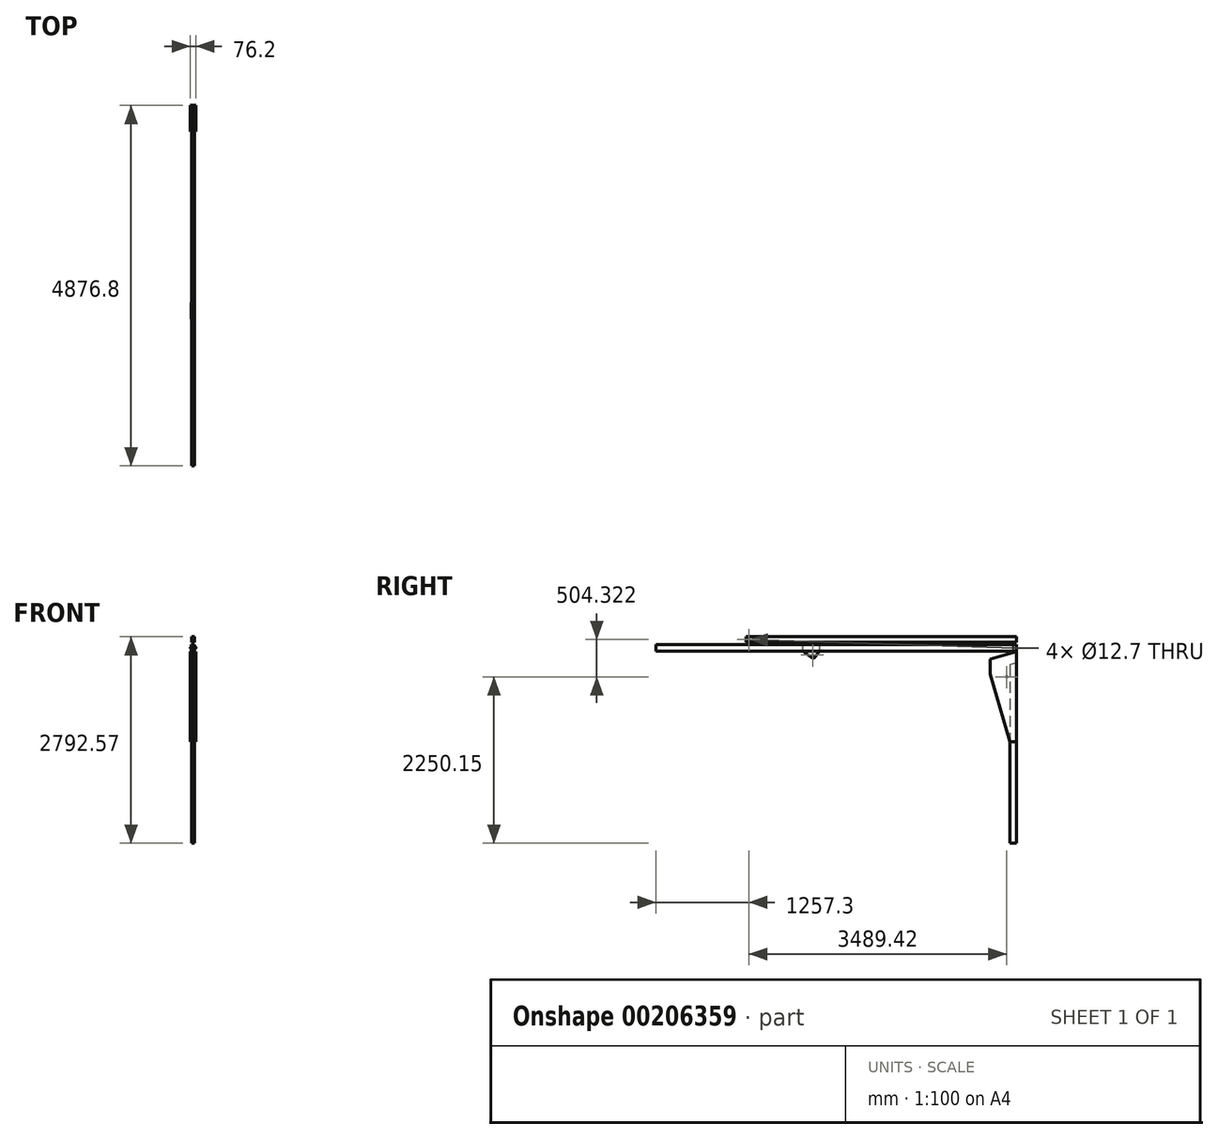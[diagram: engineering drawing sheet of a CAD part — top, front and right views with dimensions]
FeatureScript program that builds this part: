
annotation { "Feature Type Name" : "Feature", "Feature Type Description" : "" }
export const myFeature = defineFeature(function(context is Context, id is Id, definition is map)
    precondition{}
    {
        {
            var Q0;
            Q0=qCreatedBy(makeId("Right.planeOp"),FACE);
            var sketch = newSketch(context, id + "F0", { "sketchPlane" : qUnion([Q0])});
            skLineSegment(sketch, "E0", {"start": v(-355.6, 0) * mm, "end": v(0, 99.35) * mm});
            skLineSegment(sketch, "E1", {"start": v(0, 99.35) * mm, "end": v(0, -1119.85) * mm});
            skLineSegment(sketch, "E2", {"start": v(0, -1119.85) * mm, "end": v(-88.9, -1119.85) * mm});
            skLineSegment(sketch, "E3", {"start": v(-355.6, 0) * mm, "end": v(-355.6, -203.2) * mm});
            skLineSegment(sketch, "E4", {"start": v(-355.6, -203.2) * mm, "end": v(-88.9, -1119.85) * mm});
            skSolve(sketch);
        }
        {
            var Q0;
            Q0 = qSketchRegion(id + "F0", true);
            extrude(context, id + "F1", {"entities" : qUnion([Q0]), "depth" : 76.2 * mm});
        }
        {
            var Q0;
            Q0=makeQuery(id+"F1.opExtrude","SWEPT_FACE",FACE,{"disambiguationData":[OSD([sQuery(id+"F0.wireOp",EDGE,"E1")])]});
            var sketch = newSketch(context, id + "F2", { "sketchPlane" : qUnion([Q0])});
            skLineSegment(sketch, "E5.bottom", {"start": v(-57.15, 99.35) * mm, "end": v(-19.05, 99.35) * mm});
            skLineSegment(sketch, "E5.top", {"start": v(-57.15, -53.05) * mm, "end": v(-19.05, -53.05) * mm});
            skLineSegment(sketch, "E5.left", {"start": v(-57.15, 99.35) * mm, "end": v(-57.15, -53.05) * mm});
            skLineSegment(sketch, "E5.right", {"start": v(-19.05, 99.35) * mm, "end": v(-19.05, -53.05) * mm});
            skLineSegment(sketch, "E6", {"start": v(-57.15, -53.05) * mm, "end": v(-76.2, -53.05) * mm, "construction": true});
            skLineSegment(sketch, "E7", {"start": v(-19.05, -53.05) * mm, "end": v(0, -53.05) * mm, "construction": true});
            skSolve(sketch);
        }
        {
            var Q0;
            Q0 = qSketchRegion(id + "F2", true);
            var Q1;
            Q1=makeQuery(id+"F1.opExtrude","CAP_EDGE",EDGE,{"disambiguationData":[OSD([sQuery(id+"F0.wireOp",EDGE,"E0")])],"isStart":false});
            sweep(context, id + "F3", {"operationType" : NewBodyOperationType.REMOVE, "profiles" : qUnion([Q0]), "path" : qUnion([Q1])});
        }
        {
            var Q0;
            Q0=makeQuery(id+"F1.opExtrude","SWEPT_FACE",FACE,{"disambiguationData":[OSD([sQuery(id+"F0.wireOp",EDGE,"E2")])]});
            var sketch = newSketch(context, id + "F4", { "sketchPlane" : qUnion([Q0])});
            skLineSegment(sketch, "E8.bottom", {"start": v(19.05, 88.9) * mm, "end": v(57.15, 88.9) * mm});
            skLineSegment(sketch, "E8.top", {"start": v(19.05, 355.6) * mm, "end": v(57.15, 355.6) * mm});
            skLineSegment(sketch, "E8.left", {"start": v(19.05, 88.9) * mm, "end": v(19.05, 355.6) * mm});
            skLineSegment(sketch, "E8.right", {"start": v(57.15, 88.9) * mm, "end": v(57.15, 355.6) * mm});
            skLineSegment(sketch, "E9", {"start": v(0, 88.9) * mm, "end": v(19.05, 88.9) * mm, "construction": true});
            skLineSegment(sketch, "E10", {"start": v(57.15, 88.9) * mm, "end": v(76.2, 88.9) * mm, "construction": true});
            skSolve(sketch);
        }
        {
            var Q0;
            Q0 = qSketchRegion(id + "F4", true);
            extrude(context, id + "F5", {"entities" : qUnion([Q0]), "operationType" : NewBodyOperationType.REMOVE, "endBound" : BoundingType.THROUGH_ALL, "oppositeDirection" : true, "depth" : 30.48 * mm});
        }
        {
            var Q0;
            Q0=makeQuery(id+"F1.opExtrude","SWEPT_FACE",FACE,{"disambiguationData":[OSD([sQuery(id+"F0.wireOp",EDGE,"E2")])]});
            var sketch = newSketch(context, id + "F6", { "sketchPlane" : qUnion([Q0])});
            skLineSegment(sketch, "E11.bottom", {"start": v(19.05, 88.9) * mm, "end": v(57.15, 88.9) * mm});
            skLineSegment(sketch, "E11.top", {"start": v(19.05, 0) * mm, "end": v(57.15, 0) * mm});
            skLineSegment(sketch, "E11.left", {"start": v(19.05, 88.9) * mm, "end": v(19.05, 0) * mm});
            skLineSegment(sketch, "E11.right", {"start": v(57.15, 88.9) * mm, "end": v(57.15, 0) * mm});
            skSolve(sketch);
        }
        {
            var Q0;
            Q0 = qSketchRegion(id + "F6", true);
            extrude(context, id + "F7", {"entities" : qUnion([Q0]), "operationType" : NewBodyOperationType.ADD, "depth" : 1371.6 * mm});
        }
        {
            var Q0;
            Q0=makeQuery(id+"F1.opExtrude","CAP_FACE",FACE,{"disambiguationData":[OSD([sQuery(id+"F0.wireOp",EDGE,"E0"),sQuery(id+"F0.wireOp",EDGE,"E1"),sQuery(id+"F0.wireOp",EDGE,"E2"),sQuery(id+"F0.wireOp",EDGE,"E3"),sQuery(id+"F0.wireOp",EDGE,"E4")])],"isStart":true});
            var sketch = newSketch(context, id + "F8", { "sketchPlane" : qUnion([Q0])});
            skLineSegment(sketch, "E12", {"start": v(355.6, -203.2) * mm, "end": v(76.2, -203.2) * mm, "construction": true});
            skLineSegment(sketch, "E13", {"start": v(76.2, -203.2) * mm, "end": v(76.2, -279.4) * mm, "construction": true});
            skPoint(sketch, "E14.first.point", {"position": v(76.2, -241.3) * mm});
            skCircle(sketch, "E15", {"center": v(130.08, -241.3) * mm, "radius": 6.35 * mm});
            skLineSegment(sketch, "E16", {"start": v(76.2, -241.3) * mm, "end": v(38.1, -241.3) * mm, "construction": true});
            skLineSegment(sketch, "E17", {"start": v(38.1, -241.3) * mm, "end": v(38.1, -203.2) * mm, "construction": true});
            skLineSegment(sketch, "E18", {"start": v(38.1, -203.2) * mm, "end": v(76.2, -241.3) * mm, "construction": true});
            skLineSegment(sketch, "E19", {"start": v(76.2, -241.3) * mm, "end": v(130.08, -241.3) * mm, "construction": true});
            skSolve(sketch);
        }
        {
            var Q0;
            Q0 = qSketchRegion(id + "F8", true);
            extrude(context, id + "F9", {"entities" : qUnion([Q0]), "operationType" : NewBodyOperationType.REMOVE, "endBound" : BoundingType.THROUGH_ALL, "oppositeDirection" : true, "depth" : 30.48 * mm});
        }
        {
            var Q0;
            Q0=qCreatedBy(makeId("Front.planeOp"),FACE);
            var sketch = newSketch(context, id + "F10", { "sketchPlane" : qUnion([Q0])});
            skLineSegment(sketch, "E20.bottom", {"start": v(19.05, 196.76) * mm, "end": v(57.15, 196.76) * mm});
            skLineSegment(sketch, "E20.top", {"start": v(19.05, 107.86) * mm, "end": v(57.15, 107.86) * mm});
            skLineSegment(sketch, "E20.left", {"start": v(19.05, 196.76) * mm, "end": v(19.05, 107.86) * mm});
            skLineSegment(sketch, "E20.right", {"start": v(57.15, 196.76) * mm, "end": v(57.15, 107.86) * mm});
            skSolve(sketch);
        }
        {
            var Q0;
            Q0 = qSketchRegion(id + "F10", true);
            extrude(context, id + "F11", {"entities" : qUnion([Q0]), "depth" : 4876.8 * mm});
        }
        {
            var Q0;
            Q0=makeQuery(id+"F11.opExtrude","SWEPT_FACE",FACE,{"disambiguationData":[OSD([sQuery(id+"F10.wireOp",EDGE,"E20.left")])]});
            var sketch = newSketch(context, id + "F12", { "sketchPlane" : qUnion([Q0])});
            skLineSegment(sketch, "E21", {"start": v(0, 152.31) * mm, "end": v(44.45, 152.31) * mm, "construction": true});
            skLineSegment(sketch, "E22", {"start": v(44.45, 152.31) * mm, "end": v(44.45, 196.76) * mm, "construction": true});
            skCircle(sketch, "E23", {"center": v(44.45, 152.31) * mm, "radius": 6.35 * mm});
            skSolve(sketch);
        }
        {
            var Q0;
            Q0 = qSketchRegion(id + "F12", true);
            extrude(context, id + "F13", {"entities" : qUnion([Q0]), "operationType" : NewBodyOperationType.ADD, "depth" : 19.05 * mm});
        }
        {
            var Q0;
            Q0=makeQuery(id+"F11.opExtrude","SWEPT_FACE",FACE,{"disambiguationData":[OSD([sQuery(id+"F10.wireOp",EDGE,"E20.right")])]});
            var sketch = newSketch(context, id + "F14", { "sketchPlane" : qUnion([Q0])});
            skLineSegment(sketch, "E24", {"start": v(0, 152.31) * mm, "end": v(-44.45, 152.31) * mm, "construction": true});
            skLineSegment(sketch, "E25", {"start": v(-44.45, 152.31) * mm, "end": v(-44.45, 196.76) * mm, "construction": true});
            skCircle(sketch, "E26", {"center": v(-44.45, 152.31) * mm, "radius": 6.35 * mm});
            skSolve(sketch);
        }
        {
            var Q0;
            Q0 = qSketchRegion(id + "F14", true);
            extrude(context, id + "F15", {"entities" : qUnion([Q0]), "operationType" : NewBodyOperationType.ADD, "depth" : 19.05 * mm});
        }
        {
            var Q0;
            Q0=makeQuery(id+"F11.opExtrude","SWEPT_FACE",FACE,{"disambiguationData":[OSD([sQuery(id+"F10.wireOp",EDGE,"E20.left")])]});
            var sketch = newSketch(context, id + "F16", { "sketchPlane" : qUnion([Q0])});
            skLineSegment(sketch, "E27", {"start": v(2664.97, 107.86) * mm, "end": v(2748.51, 0.51) * mm});
            skLineSegment(sketch, "E28", {"start": v(2748.51, 0.51) * mm, "end": v(2886.46, 107.86) * mm});
            skLineSegment(sketch, "E29", {"start": v(2886.46, 107.86) * mm, "end": v(2886.46, 196.76) * mm});
            skLineSegment(sketch, "E30", {"start": v(2886.46, 196.76) * mm, "end": v(2664.97, 196.76) * mm});
            skLineSegment(sketch, "E31", {"start": v(2664.97, 196.76) * mm, "end": v(2664.97, 107.86) * mm});
            skLineSegment(sketch, "E32", {"start": v(2778.58, 23.91) * mm, "end": v(2755.18, 53.98) * mm, "construction": true});
            skLineSegment(sketch, "E33", {"start": v(2755.18, 53.98) * mm, "end": v(2725.11, 30.58) * mm, "construction": true});
            skLineSegment(sketch, "E34", {"start": v(2755.18, 53.98) * mm, "end": v(2755.18, 107.86) * mm, "construction": true});
            skCircle(sketch, "E35", {"center": v(2755.18, 53.98) * mm, "radius": 6.35 * mm});
            skLineSegment(sketch, "E36", {"start": v(2748.51, 0.51) * mm, "end": v(2755.18, 53.98) * mm, "construction": true});
            skSolve(sketch);
        }
        {
            var Q0;
            Q0 = qSketchRegion(id + "F16", true);
            extrude(context, id + "F17", {"entities" : qUnion([Q0]), "operationType" : NewBodyOperationType.ADD, "depth" : 6.35 * mm});
        }
        {
            var Q0;
            Q0=makeQuery(id+"F17.opExtrude","SWEPT_EDGE",EDGE,{"disambiguationData":[OSD([sQuery(id+"F16.wireOp",EDGE,"E27"),sQuery(id+"F16.wireOp",EDGE,"E28")])]});
            fillet(context, id + "F18", {"entities" : qUnion([Q0]), "radius" : 25.4 * mm, "tangentPropagation" : true, "allowEdgeOverflow" : false});
        }
        {
            var Q0;
            Q0=qCreatedBy(makeId("Front.planeOp"),FACE);
            var sketch = newSketch(context, id + "F19", { "sketchPlane" : qUnion([Q0])});
            skLineSegment(sketch, "E37.bottom", {"start": v(57.15, 301.12) * mm, "end": v(19.05, 301.12) * mm});
            skLineSegment(sketch, "E37.top", {"start": v(57.15, 224.92) * mm, "end": v(19.05, 224.92) * mm});
            skLineSegment(sketch, "E37.left", {"start": v(57.15, 301.12) * mm, "end": v(57.15, 224.92) * mm});
            skLineSegment(sketch, "E37.right", {"start": v(19.05, 301.12) * mm, "end": v(19.05, 224.92) * mm});
            skSolve(sketch);
        }
        {
            var Q0;
            Q0 = qSketchRegion(id + "F19", true);
            extrude(context, id + "F20", {"entities" : qUnion([Q0]), "depth" : 3657.6 * mm});
        }
        {
            var Q0;
            Q0=makeQuery(id+"F20.opExtrude","SWEPT_FACE",FACE,{"disambiguationData":[OSD([sQuery(id+"F19.wireOp",EDGE,"E37.right")])]});
            var sketch = newSketch(context, id + "F21", { "sketchPlane" : qUnion([Q0])});
            skLineSegment(sketch, "E38", {"start": v(3657.6, 263.02) * mm, "end": v(3619.5, 263.02) * mm, "construction": true});
            skLineSegment(sketch, "E39", {"start": v(3619.5, 263.02) * mm, "end": v(3619.5, 301.12) * mm, "construction": true});
            skCircle(sketch, "E40", {"center": v(3619.5, 263.02) * mm, "radius": 6.35 * mm});
            skSolve(sketch);
        }
        {
            var Q0;
            Q0 = qSketchRegion(id + "F21", true);
            extrude(context, id + "F22", {"entities" : qUnion([Q0]), "operationType" : NewBodyOperationType.REMOVE, "endBound" : BoundingType.THROUGH_ALL, "oppositeDirection" : true, "depth" : 30.48 * mm});
        }
    });
